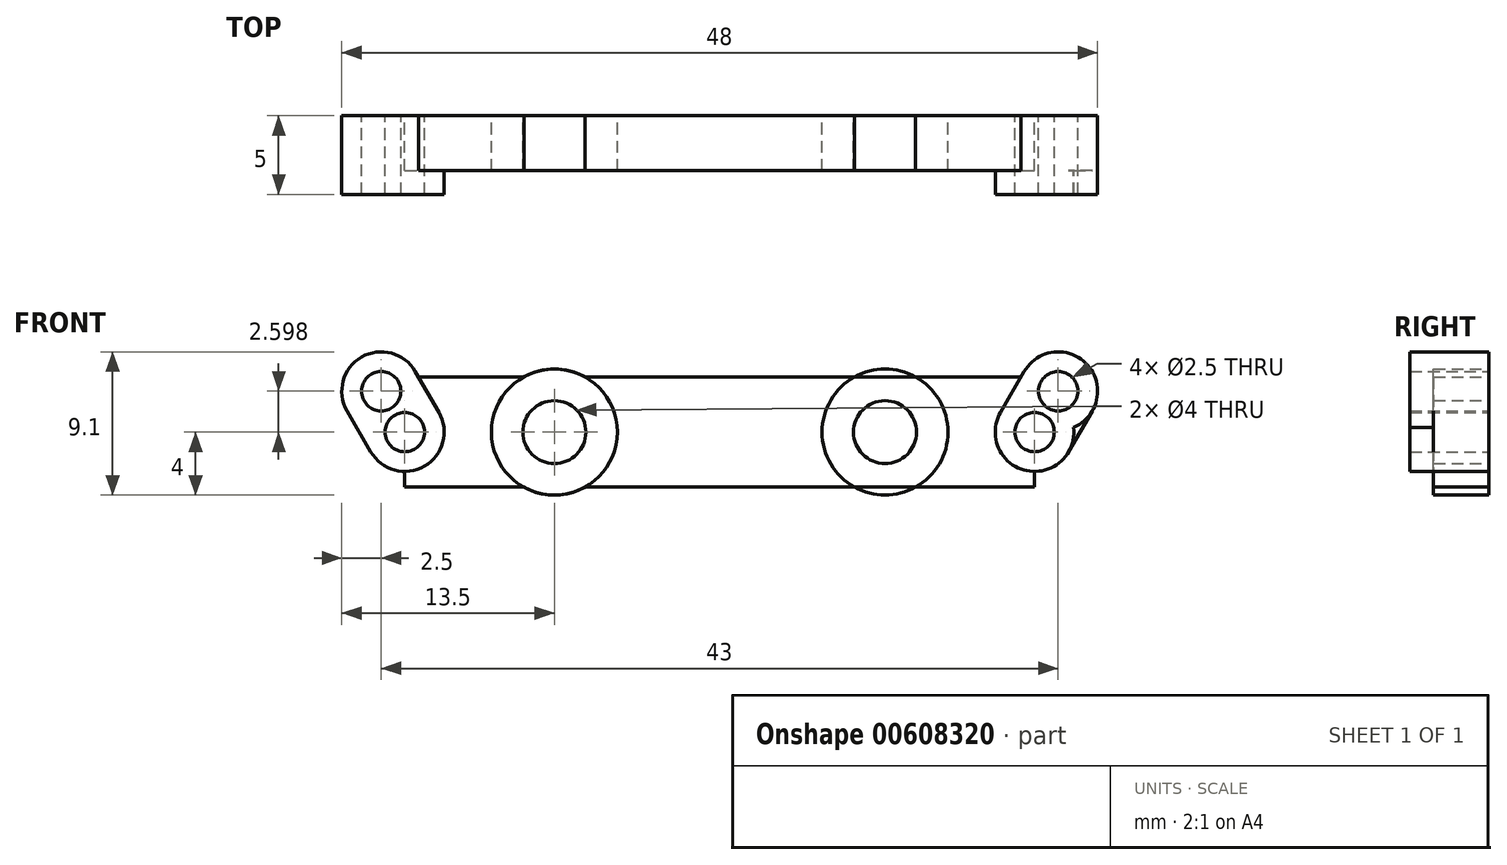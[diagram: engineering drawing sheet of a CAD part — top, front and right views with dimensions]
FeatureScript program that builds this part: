
annotation { "Feature Type Name" : "Feature", "Feature Type Description" : "" }
export const myFeature = defineFeature(function(context is Context, id is Id, definition is map)
    precondition{}
    {
        {
            var Q0;
            Q0=qCreatedBy(makeId("Front.planeOp"),FACE);
            var sketch = newSketch(context, id + "F0", { "sketchPlane" : qUnion([Q0])});
            skLineSegment(sketch, "E0.bottom", {"start": v(-20, 3.5) * mm, "end": v(20, 3.5) * mm});
            skLineSegment(sketch, "E0.top", {"start": v(-20, -3.5) * mm, "end": v(20, -3.5) * mm});
            skLineSegment(sketch, "E0.left", {"start": v(-20, 3.5) * mm, "end": v(-20, -3.5) * mm});
            skLineSegment(sketch, "E0.right", {"start": v(20, 3.5) * mm, "end": v(20, -3.5) * mm});
            skPoint(sketch, "E0.middle", {"position": v(0, 0) * mm});
            skCircle(sketch, "E1", {"center": v(-20, 0) * mm, "radius": 2.5 * mm});
            skCircle(sketch, "E2", {"center": v(-10.5, 0) * mm, "radius": 4 * mm});
            skCircle(sketch, "E3", {"center": v(-21.5, 2.6) * mm, "radius": 2.5 * mm});
            skLineSegment(sketch, "E4", {"start": v(-19.33, 3.85) * mm, "end": v(-17.83, 1.25) * mm});
            skLineSegment(sketch, "E5", {"start": v(-23.67, 1.35) * mm, "end": v(-22.17, -1.25) * mm});
            skCircle(sketch, "E6.MirrorC", {"center": v(20, 0) * mm, "radius": 2.5 * mm});
            skCircle(sketch, "E7.MirrorC", {"center": v(10.5, 0) * mm, "radius": 4 * mm});
            skCircle(sketch, "E8.MirrorC", {"center": v(21.5, 2.6) * mm, "radius": 2.5 * mm});
            skLineSegment(sketch, "E9.MirrorCS", {"start": v(19.33, 3.85) * mm, "end": v(17.83, 1.25) * mm});
            skLineSegment(sketch, "E10.MirrorCS", {"start": v(23.67, 1.35) * mm, "end": v(22.17, -1.25) * mm});
            skCircle(sketch, "E11", {"center": v(-10.5, 0) * mm, "radius": 2 * mm});
            skCircle(sketch, "E12", {"center": v(-20, 0) * mm, "radius": 1.25 * mm});
            skCircle(sketch, "E13", {"center": v(-21.5, 2.6) * mm, "radius": 1.25 * mm});
            skCircle(sketch, "E14.MirrorC", {"center": v(10.5, 0) * mm, "radius": 2 * mm});
            skCircle(sketch, "E15.MirrorC", {"center": v(20, 0) * mm, "radius": 1.25 * mm});
            skCircle(sketch, "E16.MirrorC", {"center": v(21.5, 2.6) * mm, "radius": 1.25 * mm});
            skSolve(sketch);
        }
        {
            var Q0;
            {var subQ1=sQuery(id+"F0.wireOp",EDGE,"E0.left");var subQ5=sQuery(id+"F0.wireOp",EDGE,"E0.bottom");var subQ6=makeQuery(id+"F0.imprint","INTERSECT",VERTEX,{"derivedFrom":[subQ5,subQ1]});Q0=makeQuery(id+"F0.imprint","IMPRINT",FACE,{"disambiguationData":[TD([[makeQuery(id+"F0.imprint","IMPRINT",EDGE,{"disambiguationData":[TD([[subQ6,-1.0]])],"derivedFrom":subQ5}),1.0]])]});}
            var Q1;
            {var subQ0=sQuery(id+"F0.wireOp",EDGE,"E5");Q1=makeQuery(id+"F0.imprint","IMPRINT",FACE,{"disambiguationData":[TD([[makeQuery(id+"F0.imprint","IMPRINT",EDGE,{"derivedFrom":subQ0}),1.0]])]});}
            var Q2;
            {var subQ1=sQuery(id+"F0.wireOp",EDGE,"E1");var subQ6=sQuery(id+"F0.wireOp",EDGE,"E0.left");var subQ7=makeQuery(id+"F0.imprint","INTERSECT",VERTEX,{"disambiguationData":[OD(0.0)],"derivedFrom":[subQ6,subQ1]});Q2=makeQuery(id+"F0.imprint","IMPRINT",FACE,{"disambiguationData":[TD([[makeQuery(id+"F0.imprint","IMPRINT",EDGE,{"disambiguationData":[TD([[subQ7,1.0]])],"derivedFrom":subQ6}),-1.0]])]});}
            var Q3;
            {var subQ1=sQuery(id+"F0.wireOp",EDGE,"E1");var subQ7=sQuery(id+"F0.wireOp",EDGE,"E0.left");var subQ8=makeQuery(id+"F0.imprint","INTERSECT",VERTEX,{"disambiguationData":[OD(1.0)],"derivedFrom":[subQ7,subQ1]});Q3=makeQuery(id+"F0.imprint","IMPRINT",FACE,{"disambiguationData":[TD([[makeQuery(id+"F0.imprint","IMPRINT",EDGE,{"disambiguationData":[TD([[subQ8,-1.0]])],"derivedFrom":subQ7}),-1.0]])]});}
            var Q4;
            {var subQ0=sQuery(id+"F0.wireOp",EDGE,"E1");var subQ1=sQuery(id+"F0.wireOp",EDGE,"E0.left");var subQ2=makeQuery(id+"F0.imprint","INTERSECT",VERTEX,{"disambiguationData":[OD(1.0)],"derivedFrom":[subQ1,subQ0]});Q4=makeQuery(id+"F0.imprint","IMPRINT",FACE,{"disambiguationData":[TD([[makeQuery(id+"F0.imprint","IMPRINT",EDGE,{"disambiguationData":[TD([[subQ2,-1.0]])],"derivedFrom":subQ1}),1.0]])]});}
            var Q5;
            {var subQ0=sQuery(id+"F0.wireOp",EDGE,"E0.left");var subQ1=sQuery(id+"F0.wireOp",EDGE,"E0.bottom");var subQ2=makeQuery(id+"F0.imprint","INTERSECT",VERTEX,{"derivedFrom":[subQ1,subQ0]});Q5=makeQuery(id+"F0.imprint","IMPRINT",FACE,{"disambiguationData":[TD([[makeQuery(id+"F0.imprint","IMPRINT",EDGE,{"disambiguationData":[TD([[subQ2,-1.0]])],"derivedFrom":subQ1}),-1.0]])]});}
            var Q6;
            {var subQ1=sQuery(id+"F0.wireOp",EDGE,"E1");var subQ6=sQuery(id+"F0.wireOp",EDGE,"E0.left");var subQ7=makeQuery(id+"F0.imprint","INTERSECT",VERTEX,{"disambiguationData":[OD(0.0)],"derivedFrom":[subQ6,subQ1]});Q6=makeQuery(id+"F0.imprint","IMPRINT",FACE,{"disambiguationData":[TD([[makeQuery(id+"F0.imprint","IMPRINT",EDGE,{"disambiguationData":[TD([[subQ7,1.0]])],"derivedFrom":subQ6}),1.0]])]});}
            var Q7;
            {var subQ0=sQuery(id+"F0.wireOp",EDGE,"E4");var subQ1=sQuery(id+"F0.wireOp",EDGE,"E0.bottom");var subQ2=makeQuery(id+"F0.imprint","INTERSECT",VERTEX,{"derivedFrom":[subQ1,subQ0]});Q7=makeQuery(id+"F0.imprint","IMPRINT",FACE,{"disambiguationData":[TD([[makeQuery(id+"F0.imprint","IMPRINT",EDGE,{"disambiguationData":[TD([[subQ2,1.0]])],"derivedFrom":subQ1}),-1.0]])]});}
            var Q8;
            {var subQ0=sQuery(id+"F0.wireOp",EDGE,"E4");var subQ1=sQuery(id+"F0.wireOp",EDGE,"E0.bottom");var subQ2=makeQuery(id+"F0.imprint","INTERSECT",VERTEX,{"derivedFrom":[subQ1,subQ0]});Q8=makeQuery(id+"F0.imprint","IMPRINT",FACE,{"disambiguationData":[TD([[makeQuery(id+"F0.imprint","IMPRINT",EDGE,{"disambiguationData":[TD([[subQ2,1.0]])],"derivedFrom":subQ1}),1.0]])]});}
            var Q9;
            {var subQ5=sQuery(id+"F0.wireOp",EDGE,"E4");var subQ7=sQuery(id+"F0.wireOp",EDGE,"E0.bottom");var subQ8=makeQuery(id+"F0.imprint","INTERSECT",VERTEX,{"derivedFrom":[subQ7,subQ5]});Q9=makeQuery(id+"F0.imprint","IMPRINT",FACE,{"disambiguationData":[TD([[makeQuery(id+"F0.imprint","IMPRINT",EDGE,{"disambiguationData":[TD([[subQ8,-1.0]])],"derivedFrom":subQ7}),-1.0]])]});}
            var Q10;
            Q10=makeQuery(id+"F0.imprint","IMPRINT",FACE,{"disambiguationData":[TD([[makeQuery(id+"F0.imprint","IMPRINT",EDGE,{"derivedFrom":sQuery(id+"F0.wireOp",EDGE,"E11")}),-1.0]])]});
            var Q11;
            {var subQ0=sQuery(id+"F0.wireOp",EDGE,"E2");var subQ1=sQuery(id+"F0.wireOp",EDGE,"E0.bottom");var subQ2=makeQuery(id+"F0.imprint","INTERSECT",VERTEX,{"disambiguationData":[OD(0.0)],"derivedFrom":[subQ1,subQ0]});Q11=makeQuery(id+"F0.imprint","IMPRINT",FACE,{"disambiguationData":[TD([[makeQuery(id+"F0.imprint","IMPRINT",EDGE,{"disambiguationData":[TD([[subQ2,-1.0]])],"derivedFrom":subQ1}),1.0]])]});}
            var Q12;
            {var subQ0=sQuery(id+"F0.wireOp",EDGE,"E2");var subQ1=sQuery(id+"F0.wireOp",EDGE,"E0.top");var subQ2=makeQuery(id+"F0.imprint","INTERSECT",VERTEX,{"disambiguationData":[OD(0.0)],"derivedFrom":[subQ1,subQ0]});Q12=makeQuery(id+"F0.imprint","IMPRINT",FACE,{"disambiguationData":[TD([[makeQuery(id+"F0.imprint","IMPRINT",EDGE,{"disambiguationData":[TD([[subQ2,-1.0]])],"derivedFrom":subQ1}),-1.0]])]});}
            var Q13;
            {var subQ0=sQuery(id+"F0.wireOp",EDGE,"E2");var subQ1=sQuery(id+"F0.wireOp",EDGE,"E0.bottom");var subQ2=makeQuery(id+"F0.imprint","INTERSECT",VERTEX,{"disambiguationData":[OD(1.0)],"derivedFrom":[subQ1,subQ0]});Q13=makeQuery(id+"F0.imprint","IMPRINT",FACE,{"disambiguationData":[TD([[makeQuery(id+"F0.imprint","IMPRINT",EDGE,{"disambiguationData":[TD([[subQ2,-1.0]])],"derivedFrom":subQ1}),-1.0]])]});}
            var Q14;
            {var subQ7=sQuery(id+"F0.wireOp",EDGE,"E0.bottom");var subQ9=sQuery(id+"F0.wireOp",EDGE,"E7.MirrorC");var subQ11=makeQuery(id+"F0.imprint","INTERSECT",VERTEX,{"disambiguationData":[OD(1.0)],"derivedFrom":[subQ7,subQ9]});Q14=makeQuery(id+"F0.imprint","IMPRINT",FACE,{"disambiguationData":[TD([[makeQuery(id+"F0.imprint","IMPRINT",EDGE,{"disambiguationData":[TD([[subQ11,-1.0]])],"derivedFrom":subQ7}),-1.0]])]});}
            var Q15;
            Q15=makeQuery(id+"F0.imprint","IMPRINT",FACE,{"disambiguationData":[TD([[makeQuery(id+"F0.imprint","IMPRINT",EDGE,{"derivedFrom":sQuery(id+"F0.wireOp",EDGE,"E14.MirrorC")}),1.0]])]});
            var Q16;
            {var subQ0=sQuery(id+"F0.wireOp",EDGE,"E7.MirrorC");var subQ1=sQuery(id+"F0.wireOp",EDGE,"E0.bottom");var subQ2=makeQuery(id+"F0.imprint","INTERSECT",VERTEX,{"disambiguationData":[OD(0.0)],"derivedFrom":[subQ1,subQ0]});Q16=makeQuery(id+"F0.imprint","IMPRINT",FACE,{"disambiguationData":[TD([[makeQuery(id+"F0.imprint","IMPRINT",EDGE,{"disambiguationData":[TD([[subQ2,-1.0]])],"derivedFrom":subQ1}),1.0]])]});}
            var Q17;
            {var subQ0=sQuery(id+"F0.wireOp",EDGE,"E7.MirrorC");var subQ1=sQuery(id+"F0.wireOp",EDGE,"E0.top");var subQ2=makeQuery(id+"F0.imprint","INTERSECT",VERTEX,{"disambiguationData":[OD(0.0)],"derivedFrom":[subQ1,subQ0]});Q17=makeQuery(id+"F0.imprint","IMPRINT",FACE,{"disambiguationData":[TD([[makeQuery(id+"F0.imprint","IMPRINT",EDGE,{"disambiguationData":[TD([[subQ2,-1.0]])],"derivedFrom":subQ1}),-1.0]])]});}
            var Q18;
            {var subQ0=sQuery(id+"F0.wireOp",EDGE,"E6.MirrorC");var subQ2=sQuery(id+"F0.wireOp",EDGE,"E0.right");var subQ3=makeQuery(id+"F0.imprint","INTERSECT",VERTEX,{"disambiguationData":[OD(0.0)],"derivedFrom":[subQ2,subQ0]});Q18=makeQuery(id+"F0.imprint","IMPRINT",FACE,{"disambiguationData":[TD([[makeQuery(id+"F0.imprint","IMPRINT",EDGE,{"disambiguationData":[TD([[subQ3,1.0]])],"derivedFrom":subQ2}),-1.0]])]});}
            var Q19;
            {var subQ1=sQuery(id+"F0.wireOp",EDGE,"E6.MirrorC");var subQ7=sQuery(id+"F0.wireOp",EDGE,"E0.right");var subQ8=makeQuery(id+"F0.imprint","INTERSECT",VERTEX,{"disambiguationData":[OD(1.0)],"derivedFrom":[subQ7,subQ1]});Q19=makeQuery(id+"F0.imprint","IMPRINT",FACE,{"disambiguationData":[TD([[makeQuery(id+"F0.imprint","IMPRINT",EDGE,{"disambiguationData":[TD([[subQ8,-1.0]])],"derivedFrom":subQ7}),1.0]])]});}
            var Q20;
            {var subQ0=sQuery(id+"F0.wireOp",EDGE,"E6.MirrorC");var subQ2=sQuery(id+"F0.wireOp",EDGE,"E0.right");var subQ3=makeQuery(id+"F0.imprint","INTERSECT",VERTEX,{"disambiguationData":[OD(0.0)],"derivedFrom":[subQ2,subQ0]});Q20=makeQuery(id+"F0.imprint","IMPRINT",FACE,{"disambiguationData":[TD([[makeQuery(id+"F0.imprint","IMPRINT",EDGE,{"disambiguationData":[TD([[subQ3,1.0]])],"derivedFrom":subQ2}),1.0]])]});}
            var Q21;
            {var subQ0=sQuery(id+"F0.wireOp",EDGE,"E6.MirrorC");var subQ1=sQuery(id+"F0.wireOp",EDGE,"E0.right");var subQ2=makeQuery(id+"F0.imprint","INTERSECT",VERTEX,{"disambiguationData":[OD(1.0)],"derivedFrom":[subQ1,subQ0]});Q21=makeQuery(id+"F0.imprint","IMPRINT",FACE,{"disambiguationData":[TD([[makeQuery(id+"F0.imprint","IMPRINT",EDGE,{"disambiguationData":[TD([[subQ2,-1.0]])],"derivedFrom":subQ1}),-1.0]])]});}
            var Q22;
            {var subQ1=sQuery(id+"F0.wireOp",EDGE,"E0.right");var subQ10=sQuery(id+"F0.wireOp",EDGE,"E0.bottom");var subQ11=makeQuery(id+"F0.imprint","INTERSECT",VERTEX,{"derivedFrom":[subQ10,subQ1]});Q22=makeQuery(id+"F0.imprint","IMPRINT",FACE,{"disambiguationData":[TD([[makeQuery(id+"F0.imprint","IMPRINT",EDGE,{"disambiguationData":[TD([[subQ11,1.0]])],"derivedFrom":subQ10}),1.0]])]});}
            var Q23;
            {var subQ0=sQuery(id+"F0.wireOp",EDGE,"E9.MirrorCS");var subQ1=sQuery(id+"F0.wireOp",EDGE,"E0.bottom");var subQ2=makeQuery(id+"F0.imprint","INTERSECT",VERTEX,{"derivedFrom":[subQ1,subQ0]});Q23=makeQuery(id+"F0.imprint","IMPRINT",FACE,{"disambiguationData":[TD([[makeQuery(id+"F0.imprint","IMPRINT",EDGE,{"disambiguationData":[TD([[subQ2,-1.0]])],"derivedFrom":subQ1}),-1.0]])]});}
            var Q24;
            {var subQ0=sQuery(id+"F0.wireOp",EDGE,"E9.MirrorCS");var subQ1=sQuery(id+"F0.wireOp",EDGE,"E0.bottom");var subQ2=makeQuery(id+"F0.imprint","INTERSECT",VERTEX,{"derivedFrom":[subQ1,subQ0]});Q24=makeQuery(id+"F0.imprint","IMPRINT",FACE,{"disambiguationData":[TD([[makeQuery(id+"F0.imprint","IMPRINT",EDGE,{"disambiguationData":[TD([[subQ2,-1.0]])],"derivedFrom":subQ1}),1.0]])]});}
            var Q25;
            {var subQ0=sQuery(id+"F0.wireOp",EDGE,"E0.right");var subQ1=sQuery(id+"F0.wireOp",EDGE,"E0.bottom");var subQ2=makeQuery(id+"F0.imprint","INTERSECT",VERTEX,{"derivedFrom":[subQ1,subQ0]});Q25=makeQuery(id+"F0.imprint","IMPRINT",FACE,{"disambiguationData":[TD([[makeQuery(id+"F0.imprint","IMPRINT",EDGE,{"disambiguationData":[TD([[subQ2,1.0]])],"derivedFrom":subQ1}),-1.0]])]});}
            var Q26;
            {var subQ0=sQuery(id+"F0.wireOp",EDGE,"E10.MirrorCS");Q26=makeQuery(id+"F0.imprint","IMPRINT",FACE,{"disambiguationData":[TD([[makeQuery(id+"F0.imprint","IMPRINT",EDGE,{"derivedFrom":subQ0}),-1.0]])]});}
            extrude(context, id + "F1", {"entities" : qUnion([Q0, Q1, Q2, Q3, Q4, Q5, Q6, Q7, Q8, Q9, Q10, Q11, Q12, Q13, Q14, Q15, Q16, Q17, Q18, Q19, Q20, Q21, Q22, Q23, Q24, Q25, Q26]), "depth" : 3.5 * mm, "offsetDistance" : 25 * mm});
        }
        {
            var Q0;
            Q0=makeQuery(id+"F0.imprint","IMPRINT",FACE,{"disambiguationData":[TD([[makeQuery(id+"F0.imprint","IMPRINT",EDGE,{"derivedFrom":sQuery(id+"F0.wireOp",EDGE,"E11")}),-1.0]])]});
            var Q1;
            {var subQ0=sQuery(id+"F0.wireOp",EDGE,"E2");var subQ1=sQuery(id+"F0.wireOp",EDGE,"E0.bottom");var subQ2=makeQuery(id+"F0.imprint","INTERSECT",VERTEX,{"disambiguationData":[OD(0.0)],"derivedFrom":[subQ1,subQ0]});Q1=makeQuery(id+"F0.imprint","IMPRINT",FACE,{"disambiguationData":[TD([[makeQuery(id+"F0.imprint","IMPRINT",EDGE,{"disambiguationData":[TD([[subQ2,-1.0]])],"derivedFrom":subQ1}),1.0]])]});}
            var Q2;
            {var subQ0=sQuery(id+"F0.wireOp",EDGE,"E2");var subQ1=sQuery(id+"F0.wireOp",EDGE,"E0.top");var subQ2=makeQuery(id+"F0.imprint","INTERSECT",VERTEX,{"disambiguationData":[OD(0.0)],"derivedFrom":[subQ1,subQ0]});Q2=makeQuery(id+"F0.imprint","IMPRINT",FACE,{"disambiguationData":[TD([[makeQuery(id+"F0.imprint","IMPRINT",EDGE,{"disambiguationData":[TD([[subQ2,-1.0]])],"derivedFrom":subQ1}),-1.0]])]});}
            var Q3;
            {var subQ0=sQuery(id+"F0.wireOp",EDGE,"E7.MirrorC");var subQ1=sQuery(id+"F0.wireOp",EDGE,"E0.bottom");var subQ2=makeQuery(id+"F0.imprint","INTERSECT",VERTEX,{"disambiguationData":[OD(0.0)],"derivedFrom":[subQ1,subQ0]});Q3=makeQuery(id+"F0.imprint","IMPRINT",FACE,{"disambiguationData":[TD([[makeQuery(id+"F0.imprint","IMPRINT",EDGE,{"disambiguationData":[TD([[subQ2,-1.0]])],"derivedFrom":subQ1}),1.0]])]});}
            var Q4;
            Q4=makeQuery(id+"F0.imprint","IMPRINT",FACE,{"disambiguationData":[TD([[makeQuery(id+"F0.imprint","IMPRINT",EDGE,{"derivedFrom":sQuery(id+"F0.wireOp",EDGE,"E14.MirrorC")}),1.0]])]});
            var Q5;
            {var subQ0=sQuery(id+"F0.wireOp",EDGE,"E7.MirrorC");var subQ1=sQuery(id+"F0.wireOp",EDGE,"E0.top");var subQ2=makeQuery(id+"F0.imprint","INTERSECT",VERTEX,{"disambiguationData":[OD(0.0)],"derivedFrom":[subQ1,subQ0]});Q5=makeQuery(id+"F0.imprint","IMPRINT",FACE,{"disambiguationData":[TD([[makeQuery(id+"F0.imprint","IMPRINT",EDGE,{"disambiguationData":[TD([[subQ2,-1.0]])],"derivedFrom":subQ1}),-1.0]])]});}
            extrude(context, id + "F2", {"entities" : qUnion([Q0, Q1, Q2, Q3, Q4, Q5]), "depth" : 3.5 * mm, "offsetDistance" : 25 * mm});
        }
        {
            var Q0;
            {var subQ1=sQuery(id+"F0.wireOp",EDGE,"E0.left");var subQ5=sQuery(id+"F0.wireOp",EDGE,"E0.bottom");var subQ6=makeQuery(id+"F0.imprint","INTERSECT",VERTEX,{"derivedFrom":[subQ5,subQ1]});Q0=makeQuery(id+"F0.imprint","IMPRINT",FACE,{"disambiguationData":[TD([[makeQuery(id+"F0.imprint","IMPRINT",EDGE,{"disambiguationData":[TD([[subQ6,-1.0]])],"derivedFrom":subQ5}),1.0]])]});}
            var Q1;
            {var subQ1=sQuery(id+"F0.wireOp",EDGE,"E1");var subQ7=sQuery(id+"F0.wireOp",EDGE,"E0.left");var subQ8=makeQuery(id+"F0.imprint","INTERSECT",VERTEX,{"disambiguationData":[OD(1.0)],"derivedFrom":[subQ7,subQ1]});Q1=makeQuery(id+"F0.imprint","IMPRINT",FACE,{"disambiguationData":[TD([[makeQuery(id+"F0.imprint","IMPRINT",EDGE,{"disambiguationData":[TD([[subQ8,-1.0]])],"derivedFrom":subQ7}),-1.0]])]});}
            var Q2;
            {var subQ1=sQuery(id+"F0.wireOp",EDGE,"E1");var subQ6=sQuery(id+"F0.wireOp",EDGE,"E0.left");var subQ7=makeQuery(id+"F0.imprint","INTERSECT",VERTEX,{"disambiguationData":[OD(0.0)],"derivedFrom":[subQ6,subQ1]});Q2=makeQuery(id+"F0.imprint","IMPRINT",FACE,{"disambiguationData":[TD([[makeQuery(id+"F0.imprint","IMPRINT",EDGE,{"disambiguationData":[TD([[subQ7,1.0]])],"derivedFrom":subQ6}),-1.0]])]});}
            var Q3;
            {var subQ1=sQuery(id+"F0.wireOp",EDGE,"E1");var subQ6=sQuery(id+"F0.wireOp",EDGE,"E0.left");var subQ7=makeQuery(id+"F0.imprint","INTERSECT",VERTEX,{"disambiguationData":[OD(0.0)],"derivedFrom":[subQ6,subQ1]});Q3=makeQuery(id+"F0.imprint","IMPRINT",FACE,{"disambiguationData":[TD([[makeQuery(id+"F0.imprint","IMPRINT",EDGE,{"disambiguationData":[TD([[subQ7,1.0]])],"derivedFrom":subQ6}),1.0]])]});}
            var Q4;
            {var subQ0=sQuery(id+"F0.wireOp",EDGE,"E1");var subQ1=sQuery(id+"F0.wireOp",EDGE,"E0.left");var subQ2=makeQuery(id+"F0.imprint","INTERSECT",VERTEX,{"disambiguationData":[OD(1.0)],"derivedFrom":[subQ1,subQ0]});Q4=makeQuery(id+"F0.imprint","IMPRINT",FACE,{"disambiguationData":[TD([[makeQuery(id+"F0.imprint","IMPRINT",EDGE,{"disambiguationData":[TD([[subQ2,-1.0]])],"derivedFrom":subQ1}),1.0]])]});}
            var Q5;
            {var subQ0=sQuery(id+"F0.wireOp",EDGE,"E4");var subQ1=sQuery(id+"F0.wireOp",EDGE,"E0.bottom");var subQ2=makeQuery(id+"F0.imprint","INTERSECT",VERTEX,{"derivedFrom":[subQ1,subQ0]});Q5=makeQuery(id+"F0.imprint","IMPRINT",FACE,{"disambiguationData":[TD([[makeQuery(id+"F0.imprint","IMPRINT",EDGE,{"disambiguationData":[TD([[subQ2,1.0]])],"derivedFrom":subQ1}),-1.0]])]});}
            var Q6;
            {var subQ0=sQuery(id+"F0.wireOp",EDGE,"E0.left");var subQ1=sQuery(id+"F0.wireOp",EDGE,"E0.bottom");var subQ2=makeQuery(id+"F0.imprint","INTERSECT",VERTEX,{"derivedFrom":[subQ1,subQ0]});Q6=makeQuery(id+"F0.imprint","IMPRINT",FACE,{"disambiguationData":[TD([[makeQuery(id+"F0.imprint","IMPRINT",EDGE,{"disambiguationData":[TD([[subQ2,-1.0]])],"derivedFrom":subQ1}),-1.0]])]});}
            var Q7;
            {var subQ0=sQuery(id+"F0.wireOp",EDGE,"E4");var subQ1=sQuery(id+"F0.wireOp",EDGE,"E0.bottom");var subQ2=makeQuery(id+"F0.imprint","INTERSECT",VERTEX,{"derivedFrom":[subQ1,subQ0]});Q7=makeQuery(id+"F0.imprint","IMPRINT",FACE,{"disambiguationData":[TD([[makeQuery(id+"F0.imprint","IMPRINT",EDGE,{"disambiguationData":[TD([[subQ2,1.0]])],"derivedFrom":subQ1}),1.0]])]});}
            var Q8;
            {var subQ0=sQuery(id+"F0.wireOp",EDGE,"E5");Q8=makeQuery(id+"F0.imprint","IMPRINT",FACE,{"disambiguationData":[TD([[makeQuery(id+"F0.imprint","IMPRINT",EDGE,{"derivedFrom":subQ0}),1.0]])]});}
            var Q9;
            {var subQ0=sQuery(id+"F0.wireOp",EDGE,"E6.MirrorC");var subQ2=sQuery(id+"F0.wireOp",EDGE,"E0.right");var subQ3=makeQuery(id+"F0.imprint","INTERSECT",VERTEX,{"disambiguationData":[OD(0.0)],"derivedFrom":[subQ2,subQ0]});Q9=makeQuery(id+"F0.imprint","IMPRINT",FACE,{"disambiguationData":[TD([[makeQuery(id+"F0.imprint","IMPRINT",EDGE,{"disambiguationData":[TD([[subQ3,1.0]])],"derivedFrom":subQ2}),-1.0]])]});}
            var Q10;
            {var subQ0=sQuery(id+"F0.wireOp",EDGE,"E6.MirrorC");var subQ2=sQuery(id+"F0.wireOp",EDGE,"E0.right");var subQ3=makeQuery(id+"F0.imprint","INTERSECT",VERTEX,{"disambiguationData":[OD(0.0)],"derivedFrom":[subQ2,subQ0]});Q10=makeQuery(id+"F0.imprint","IMPRINT",FACE,{"disambiguationData":[TD([[makeQuery(id+"F0.imprint","IMPRINT",EDGE,{"disambiguationData":[TD([[subQ3,1.0]])],"derivedFrom":subQ2}),1.0]])]});}
            var Q11;
            {var subQ1=sQuery(id+"F0.wireOp",EDGE,"E6.MirrorC");var subQ7=sQuery(id+"F0.wireOp",EDGE,"E0.right");var subQ8=makeQuery(id+"F0.imprint","INTERSECT",VERTEX,{"disambiguationData":[OD(1.0)],"derivedFrom":[subQ7,subQ1]});Q11=makeQuery(id+"F0.imprint","IMPRINT",FACE,{"disambiguationData":[TD([[makeQuery(id+"F0.imprint","IMPRINT",EDGE,{"disambiguationData":[TD([[subQ8,-1.0]])],"derivedFrom":subQ7}),1.0]])]});}
            var Q12;
            {var subQ1=sQuery(id+"F0.wireOp",EDGE,"E0.right");var subQ10=sQuery(id+"F0.wireOp",EDGE,"E0.bottom");var subQ11=makeQuery(id+"F0.imprint","INTERSECT",VERTEX,{"derivedFrom":[subQ10,subQ1]});Q12=makeQuery(id+"F0.imprint","IMPRINT",FACE,{"disambiguationData":[TD([[makeQuery(id+"F0.imprint","IMPRINT",EDGE,{"disambiguationData":[TD([[subQ11,1.0]])],"derivedFrom":subQ10}),1.0]])]});}
            var Q13;
            {var subQ0=sQuery(id+"F0.wireOp",EDGE,"E9.MirrorCS");var subQ1=sQuery(id+"F0.wireOp",EDGE,"E0.bottom");var subQ2=makeQuery(id+"F0.imprint","INTERSECT",VERTEX,{"derivedFrom":[subQ1,subQ0]});Q13=makeQuery(id+"F0.imprint","IMPRINT",FACE,{"disambiguationData":[TD([[makeQuery(id+"F0.imprint","IMPRINT",EDGE,{"disambiguationData":[TD([[subQ2,-1.0]])],"derivedFrom":subQ1}),-1.0]])]});}
            var Q14;
            {var subQ0=sQuery(id+"F0.wireOp",EDGE,"E0.right");var subQ1=sQuery(id+"F0.wireOp",EDGE,"E0.bottom");var subQ2=makeQuery(id+"F0.imprint","INTERSECT",VERTEX,{"derivedFrom":[subQ1,subQ0]});Q14=makeQuery(id+"F0.imprint","IMPRINT",FACE,{"disambiguationData":[TD([[makeQuery(id+"F0.imprint","IMPRINT",EDGE,{"disambiguationData":[TD([[subQ2,1.0]])],"derivedFrom":subQ1}),-1.0]])]});}
            var Q15;
            {var subQ0=sQuery(id+"F0.wireOp",EDGE,"E9.MirrorCS");var subQ1=sQuery(id+"F0.wireOp",EDGE,"E0.bottom");var subQ2=makeQuery(id+"F0.imprint","INTERSECT",VERTEX,{"derivedFrom":[subQ1,subQ0]});Q15=makeQuery(id+"F0.imprint","IMPRINT",FACE,{"disambiguationData":[TD([[makeQuery(id+"F0.imprint","IMPRINT",EDGE,{"disambiguationData":[TD([[subQ2,-1.0]])],"derivedFrom":subQ1}),1.0]])]});}
            var Q16;
            {var subQ0=sQuery(id+"F0.wireOp",EDGE,"E6.MirrorC");var subQ1=sQuery(id+"F0.wireOp",EDGE,"E0.right");var subQ2=makeQuery(id+"F0.imprint","INTERSECT",VERTEX,{"disambiguationData":[OD(1.0)],"derivedFrom":[subQ1,subQ0]});Q16=makeQuery(id+"F0.imprint","IMPRINT",FACE,{"disambiguationData":[TD([[makeQuery(id+"F0.imprint","IMPRINT",EDGE,{"disambiguationData":[TD([[subQ2,-1.0]])],"derivedFrom":subQ1}),-1.0]])]});}
            extrude(context, id + "F3", {"entities" : qUnion([Q0, Q1, Q2, Q3, Q4, Q5, Q6, Q7, Q8, Q9, Q10, Q11, Q12, Q13, Q14, Q15, Q16]), "operationType" : NewBodyOperationType.ADD, "depth" : 5 * mm, "offsetDistance" : 25 * mm});
        }
    });
